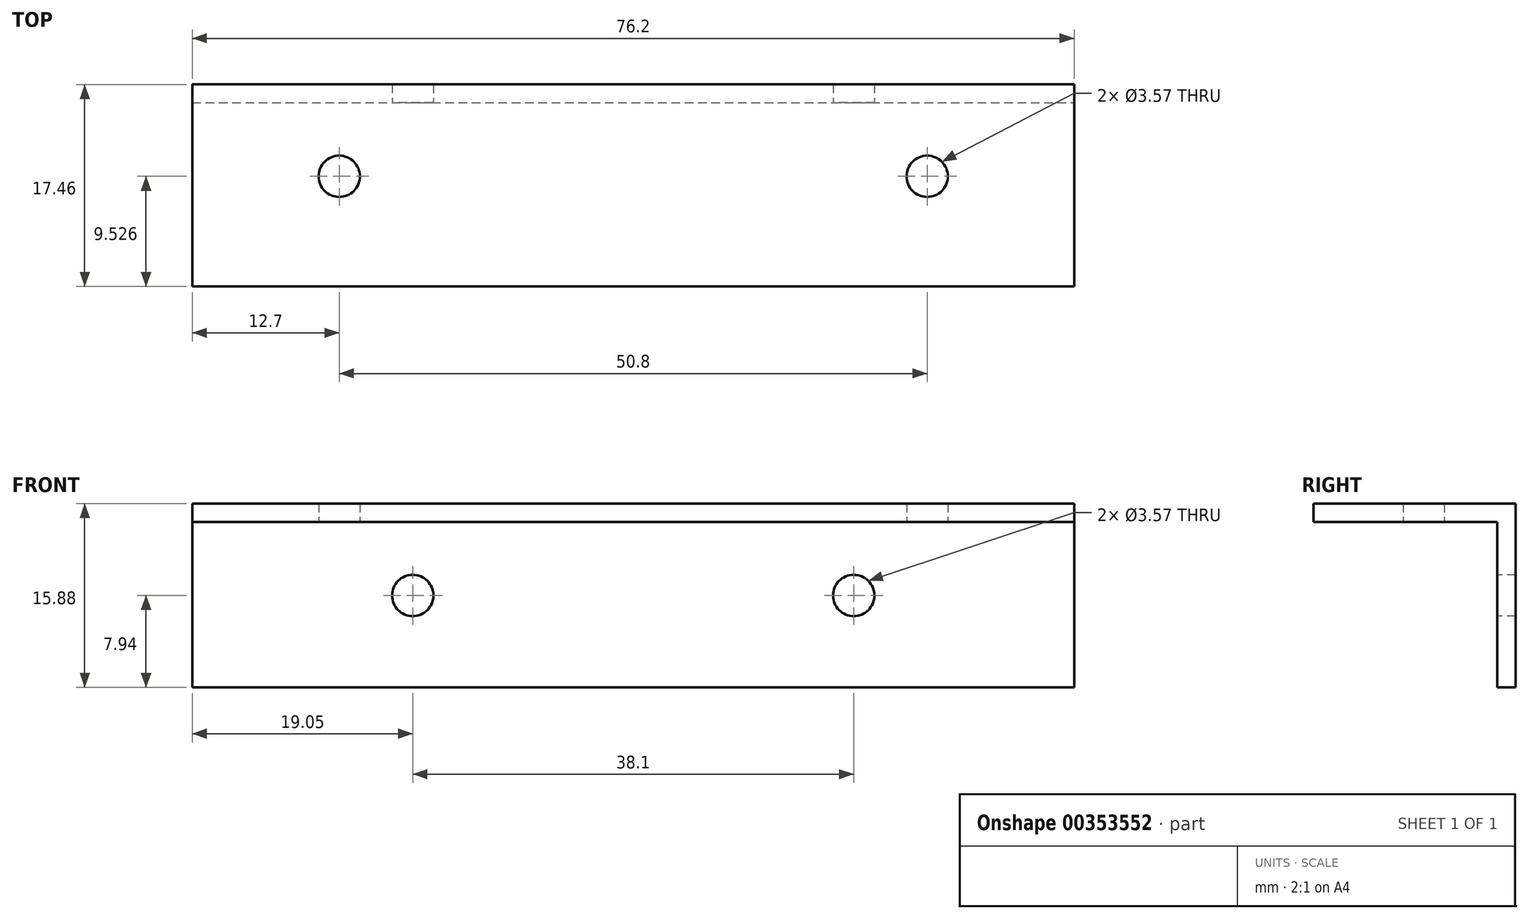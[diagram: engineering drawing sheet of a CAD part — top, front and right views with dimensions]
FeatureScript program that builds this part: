
annotation { "Feature Type Name" : "Feature", "Feature Type Description" : "" }
export const myFeature = defineFeature(function(context is Context, id is Id, definition is map)
    precondition{}
    {
        {
            var Q0;
            Q0=qCreatedBy(makeId("Front.planeOp"),FACE);
            var sketch = newSketch(context, id + "F0", { "sketchPlane" : qUnion([Q0])});
            skLineSegment(sketch, "E0.bottom", {"start": v(-38.1, 7.94) * mm, "end": v(38.1, 7.94) * mm});
            skLineSegment(sketch, "E0.top", {"start": v(-38.1, -7.94) * mm, "end": v(38.1, -7.94) * mm});
            skLineSegment(sketch, "E0.left", {"start": v(-38.1, 7.94) * mm, "end": v(-38.1, -7.94) * mm});
            skLineSegment(sketch, "E0.right", {"start": v(38.1, 7.94) * mm, "end": v(38.1, -7.94) * mm});
            skPoint(sketch, "E0.middle", {"position": v(0, 0) * mm});
            skSolve(sketch);
        }
        {
            var Q0;
            Q0 = qSketchRegion(id + "F0", true);
            extrude(context, id + "F1", {"entities" : qUnion([Q0]), "depth" : 1.59 * mm, "symmetric" : true});
        }
        {
            var Q0;
            Q0=makeQuery(id+"F1.opExtrude","CAP_FACE",FACE,{"disambiguationData":[OSD([sQuery(id+"F0.wireOp",EDGE,"E0.bottom"),sQuery(id+"F0.wireOp",EDGE,"E0.top"),sQuery(id+"F0.wireOp",EDGE,"E0.left"),sQuery(id+"F0.wireOp",EDGE,"E0.right")])],"isStart":false});
            var sketch = newSketch(context, id + "F2", { "sketchPlane" : qUnion([Q0])});
            skCircle(sketch, "E1", {"center": v(-19.05, 0) * mm, "radius": 1.79 * mm});
            skSolve(sketch);
        }
        {
            var Q0;
            Q0 = qSketchRegion(id + "F2", true);
            extrude(context, id + "F3", {"entities" : qUnion([Q0]), "operationType" : NewBodyOperationType.REMOVE, "endBound" : BoundingType.THROUGH_ALL, "oppositeDirection" : true, "depth" : 25.4 * mm});
        }
        {
            var Q0;
            Q0=makeQuery(id+"F1.opExtrude","CAP_FACE",FACE,{"disambiguationData":[OSD([sQuery(id+"F0.wireOp",EDGE,"E0.bottom"),sQuery(id+"F0.wireOp",EDGE,"E0.top"),sQuery(id+"F0.wireOp",EDGE,"E0.left"),sQuery(id+"F0.wireOp",EDGE,"E0.right")])],"isStart":false});
            var sketch = newSketch(context, id + "F4", { "sketchPlane" : qUnion([Q0])});
            skCircle(sketch, "E2", {"center": v(19.05, 0) * mm, "radius": 1.79 * mm});
            skSolve(sketch);
        }
        {
            var Q0;
            Q0 = qSketchRegion(id + "F4", true);
            extrude(context, id + "F5", {"entities" : qUnion([Q0]), "operationType" : NewBodyOperationType.REMOVE, "endBound" : BoundingType.THROUGH_ALL, "oppositeDirection" : true, "depth" : 25.4 * mm});
        }
        {
            var Q0;
            Q0=makeQuery(id+"F1.opExtrude","CAP_FACE",FACE,{"disambiguationData":[OSD([sQuery(id+"F0.wireOp",EDGE,"E0.bottom"),sQuery(id+"F0.wireOp",EDGE,"E0.top"),sQuery(id+"F0.wireOp",EDGE,"E0.left"),sQuery(id+"F0.wireOp",EDGE,"E0.right")])],"isStart":false});
            var sketch = newSketch(context, id + "F6", { "sketchPlane" : qUnion([Q0])});
            skLineSegment(sketch, "E3.bottom", {"start": v(-38.1, 7.94) * mm, "end": v(38.1, 7.94) * mm});
            skLineSegment(sketch, "E3.top", {"start": v(-38.1, 6.35) * mm, "end": v(38.1, 6.35) * mm});
            skLineSegment(sketch, "E3.left", {"start": v(-38.1, 7.94) * mm, "end": v(-38.1, 6.35) * mm});
            skLineSegment(sketch, "E3.right", {"start": v(38.1, 7.94) * mm, "end": v(38.1, 6.35) * mm});
            skSolve(sketch);
        }
        {
            var Q0;
            Q0 = qSketchRegion(id + "F6", true);
            extrude(context, id + "F7", {"entities" : qUnion([Q0]), "operationType" : NewBodyOperationType.ADD, "depth" : 15.88 * mm});
        }
        {
            var Q0;
            Q0=makeQuery(id+"F7.opExtrude","SWEPT_FACE",FACE,{"disambiguationData":[OSD([sQuery(id+"F6.wireOp",EDGE,"E3.top")])]});
            var sketch = newSketch(context, id + "F8", { "sketchPlane" : qUnion([Q0])});
            skCircle(sketch, "E4", {"center": v(-25.4, 7.14) * mm, "radius": 1.79 * mm});
            skSolve(sketch);
        }
        {
            var Q0;
            Q0 = qSketchRegion(id + "F8", true);
            extrude(context, id + "F9", {"entities" : qUnion([Q0]), "operationType" : NewBodyOperationType.REMOVE, "endBound" : BoundingType.THROUGH_ALL, "oppositeDirection" : true, "depth" : 25.4 * mm});
        }
        {
            var Q0;
            Q0=makeQuery(id+"F7.opExtrude","SWEPT_FACE",FACE,{"disambiguationData":[OSD([sQuery(id+"F6.wireOp",EDGE,"E3.top")])]});
            var sketch = newSketch(context, id + "F10", { "sketchPlane" : qUnion([Q0])});
            skCircle(sketch, "E5", {"center": v(25.4, 7.14) * mm, "radius": 1.79 * mm});
            skSolve(sketch);
        }
        {
            var Q0;
            Q0 = qSketchRegion(id + "F10", true);
            extrude(context, id + "F11", {"entities" : qUnion([Q0]), "operationType" : NewBodyOperationType.REMOVE, "endBound" : BoundingType.THROUGH_ALL, "oppositeDirection" : true, "depth" : 25.4 * mm});
        }
    });
